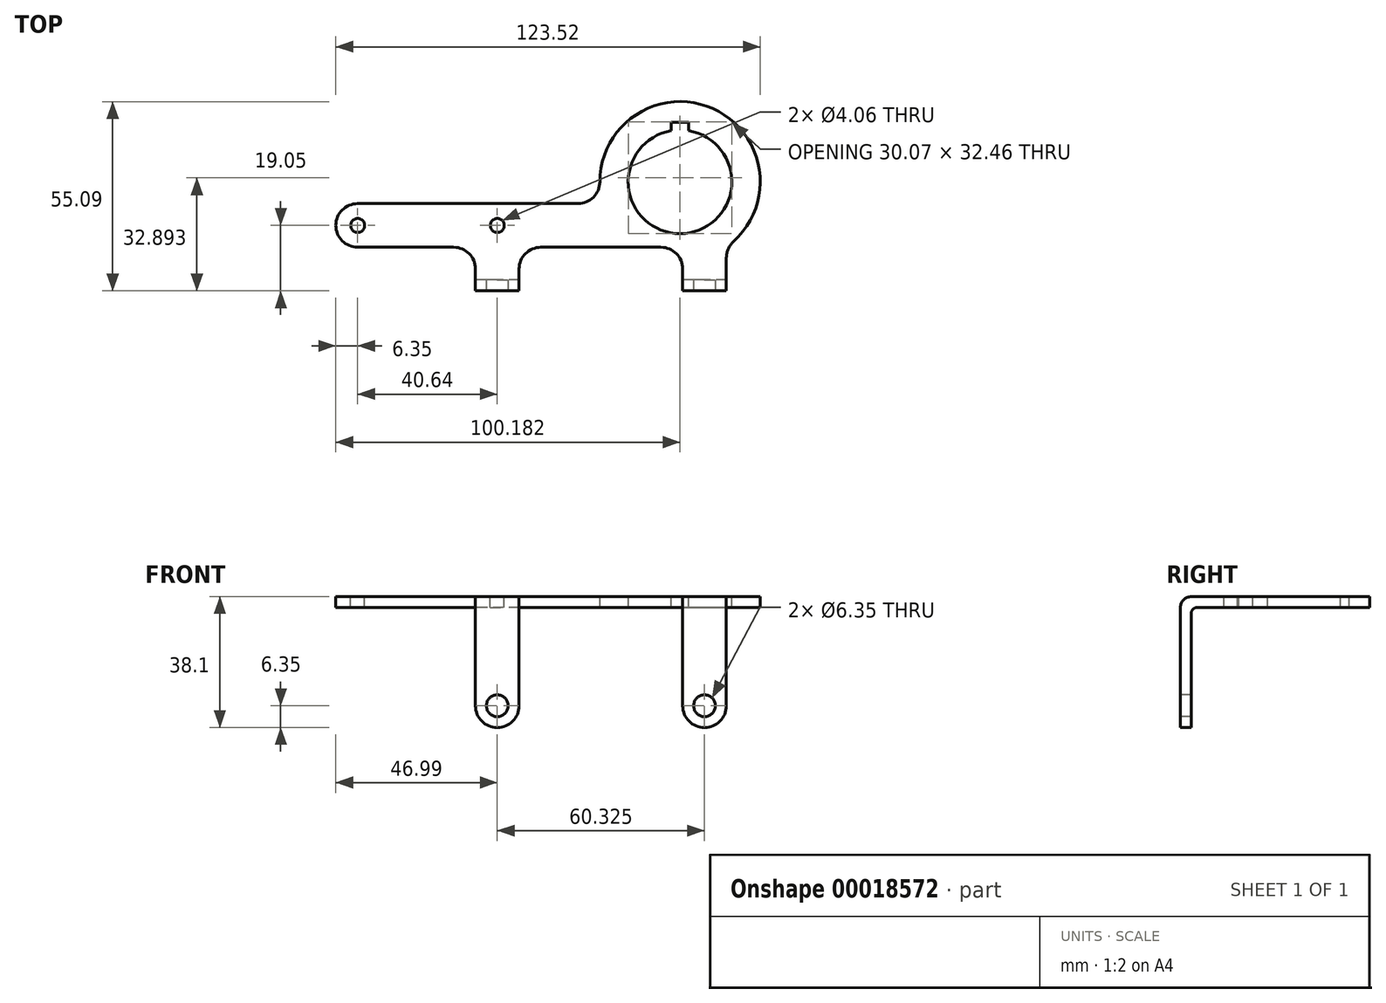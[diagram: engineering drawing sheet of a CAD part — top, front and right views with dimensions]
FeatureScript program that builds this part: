
annotation { "Feature Type Name" : "Feature", "Feature Type Description" : "" }
export const myFeature = defineFeature(function(context is Context, id is Id, definition is map)
    precondition{}
    {
        {
            var Q0;
            Q0=qCreatedBy(makeId("Right.planeOp"),FACE);
            var sketch = newSketch(context, id + "F0", { "sketchPlane" : qUnion([Q0])});
            skLineSegment(sketch, "E0", {"start": v(0, 0) * mm, "end": v(0, 38.1) * mm});
            skLineSegment(sketch, "E1", {"start": v(0, 38.1) * mm, "end": v(57.15, 38.1) * mm});
            skLineSegment(sketch, "E2", {"start": v(57.15, 38.1) * mm, "end": v(57.15, 34.93) * mm});
            skLineSegment(sketch, "E3", {"start": v(57.15, 34.93) * mm, "end": v(3.17, 34.93) * mm});
            skLineSegment(sketch, "E4", {"start": v(3.18, 34.93) * mm, "end": v(3.18, 0) * mm});
            skLineSegment(sketch, "E5", {"start": v(3.17, 0) * mm, "end": v(0, 0) * mm});
            skPoint(sketch, "E6.visualSharp", {"position": v(0, 38.1) * mm});
            skSolve(sketch);
        }
        {
            var Q0;
            Q0 = qSketchRegion(id + "F0", true);
            extrude(context, id + "F1", {"entities" : qUnion([Q0]), "depth" : 124.2 * mm});
        }
        {
            var Q0;
            Q0=makeQuery(id+"F1.opExtrude","SWEPT_EDGE",EDGE,{"disambiguationData":[OSD([sQuery(id+"F0.wireOp",EDGE,"E0"),sQuery(id+"F0.wireOp",EDGE,"E1")])]});
            fillet(context, id + "F2", {"entities" : qUnion([Q0]), "radius" : 3.17 * mm, "tangentPropagation" : true, "allowEdgeOverflow" : false});
        }
        {
            var Q0;
            Q0=makeQuery(id+"F1.opExtrude","SWEPT_EDGE",EDGE,{"disambiguationData":[OSD([sQuery(id+"F0.wireOp",EDGE,"E3"),sQuery(id+"F0.wireOp",EDGE,"E4")])]});
            fillet(context, id + "F3", {"entities" : qUnion([Q0]), "radius" : 1.59 * mm, "tangentPropagation" : true, "allowEdgeOverflow" : false});
        }
        {
            var Q0;
            Q0=makeQuery(id+"F1.opExtrude","SWEPT_FACE",FACE,{"disambiguationData":[OSD([sQuery(id+"F0.wireOp",EDGE,"E0")])]});
            var sketch = newSketch(context, id + "F4", { "sketchPlane" : qUnion([Q0])});
            skCircle(sketch, "E7", {"center": v(107.31, 6.35) * mm, "radius": 3.18 * mm});
            skCircle(sketch, "E8", {"center": v(46.99, 6.35) * mm, "radius": 3.18 * mm});
            skSolve(sketch);
        }
        {
            var Q0;
            Q0 = qSketchRegion(id + "F4", true);
            extrude(context, id + "F5", {"entities" : qUnion([Q0]), "operationType" : NewBodyOperationType.REMOVE, "endBound" : BoundingType.THROUGH_ALL, "oppositeDirection" : true, "depth" : 25.4 * mm});
        }
        {
            var Q0;
            Q0=qCreatedBy(makeId("Front.planeOp"),FACE);
            var sketch = newSketch(context, id + "F6", { "sketchPlane" : qUnion([Q0])});
            skLineSegment(sketch, "E9.bottom", {"start": v(-2.54, -2.54) * mm, "end": v(40.64, -2.54) * mm});
            skLineSegment(sketch, "E9.top", {"start": v(-2.54, 60.96) * mm, "end": v(40.64, 60.96) * mm});
            skLineSegment(sketch, "E9.left", {"start": v(-2.54, -2.54) * mm, "end": v(-2.54, 60.96) * mm});
            skLineSegment(sketch, "E9.right", {"start": v(40.64, -2.54) * mm, "end": v(40.64, 60.96) * mm});
            skLineSegment(sketch, "E10.bottom", {"start": v(53.34, -2.54) * mm, "end": v(100.97, -2.54) * mm});
            skLineSegment(sketch, "E10.top", {"start": v(53.34, 60.96) * mm, "end": v(100.97, 60.96) * mm});
            skLineSegment(sketch, "E10.left", {"start": v(53.34, -2.54) * mm, "end": v(53.34, 60.96) * mm});
            skLineSegment(sketch, "E10.right", {"start": v(100.97, -2.54) * mm, "end": v(100.97, 60.96) * mm});
            skLineSegment(sketch, "E11.bottom", {"start": v(113.67, -2.54) * mm, "end": v(126.37, -2.54) * mm});
            skLineSegment(sketch, "E11.top", {"start": v(113.67, 60.96) * mm, "end": v(126.37, 60.96) * mm});
            skLineSegment(sketch, "E11.left", {"start": v(113.67, -2.54) * mm, "end": v(113.67, 60.96) * mm});
            skLineSegment(sketch, "E11.right", {"start": v(126.37, -2.54) * mm, "end": v(126.37, 60.96) * mm});
            skSolve(sketch);
        }
        {
            var Q0;
            Q0 = qSketchRegion(id + "F6", true);
            extrude(context, id + "F7", {"entities" : qUnion([Q0]), "operationType" : NewBodyOperationType.REMOVE, "oppositeDirection" : true, "depth" : 12.7 * mm});
        }
        {
            var Q0;
            Q0=makeQuery(id+"F1.opExtrude","SWEPT_FACE",FACE,{"disambiguationData":[OSD([sQuery(id+"F0.wireOp",EDGE,"E1")])]});
            var sketch = newSketch(context, id + "F8", { "sketchPlane" : qUnion([Q0])});
            skCircle(sketch, "E12", {"center": v(6.35, 19.05) * mm, "radius": 2.03 * mm});
            skCircle(sketch, "E13", {"center": v(47, 19.05) * mm, "radius": 2.03 * mm});
            skArc(sketch, "E14", {"start": v(97.64, 46.62) * mm, "mid": v(100.18, 16.66) * mm, "end": v(102.72, 46.62) * mm});
            skLineSegment(sketch, "E15", {"start": v(100.18, 31.75) * mm, "end": v(100.18, 54.13) * mm, "construction": true});
            skLineSegment(sketch, "E16", {"start": v(100.18, 49.12) * mm, "end": v(102.72, 49.12) * mm});
            skLineSegment(sketch, "E17", {"start": v(102.72, 49.12) * mm, "end": v(102.72, 46.62) * mm});
            skLineSegment(sketch, "E18.MirrorCS", {"start": v(100.18, 49.12) * mm, "end": v(97.64, 49.12) * mm});
            skLineSegment(sketch, "E19.MirrorCS", {"start": v(97.64, 49.12) * mm, "end": v(97.64, 46.62) * mm});
            skSolve(sketch);
        }
        {
            var Q0;
            Q0 = qSketchRegion(id + "F8", true);
            extrude(context, id + "F9", {"entities" : qUnion([Q0]), "operationType" : NewBodyOperationType.REMOVE, "endBound" : BoundingType.THROUGH_ALL, "oppositeDirection" : true, "depth" : 25.4 * mm});
        }
        {
            var Q0;
            Q0=makeQuery(id+"F1.opExtrude","SWEPT_FACE",FACE,{"disambiguationData":[OSD([sQuery(id+"F0.wireOp",EDGE,"E1")])]});
            var sketch = newSketch(context, id + "F10", { "sketchPlane" : qUnion([Q0])});
            skLineSegment(sketch, "E20.bottom", {"start": v(-2.54, 63.5) * mm, "end": v(127, 63.5) * mm});
            skLineSegment(sketch, "E20.top", {"start": v(-2.54, 25.4) * mm, "end": v(77.72, 25.4) * mm});
            skLineSegment(sketch, "E20.left", {"start": v(-2.54, 63.5) * mm, "end": v(-2.54, 25.4) * mm});
            skArc(sketch, "E21", {"start": v(113.67, 12.7) * mm, "mid": v(107.96, 53.76) * mm, "end": v(77.72, 25.4) * mm});
            skLineSegment(sketch, "E22", {"start": v(113.67, 12.7) * mm, "end": v(113.67, 6.35) * mm});
            skLineSegment(sketch, "E23", {"start": v(113.67, 6.35) * mm, "end": v(127, 6.35) * mm});
            skLineSegment(sketch, "E24", {"start": v(127, 6.35) * mm, "end": v(127, 63.5) * mm});
            skSolve(sketch);
        }
        {
            var Q0;
            Q0 = qSketchRegion(id + "F10", true);
            extrude(context, id + "F11", {"entities" : qUnion([Q0]), "operationType" : NewBodyOperationType.REMOVE, "endBound" : BoundingType.THROUGH_ALL, "oppositeDirection" : true, "depth" : 25.4 * mm});
        }
        {
            var Q0;
            Q0=makeQuery(id+"F7.boolean.opBoolean","INTERSECT",EDGE,{"derivedFrom":[makeQuery(id+"F1.opExtrude","SWEPT_FACE",FACE,{"disambiguationData":[OSD([sQuery(id+"F0.wireOp",EDGE,"E5")])]}),makeQuery(id+"F7.opExtrude","SWEPT_FACE",FACE,{"disambiguationData":[OSD([sQuery(id+"F6.wireOp",EDGE,"E10.left")])]})]});
            var Q1;
            Q1=makeQuery(id+"F7.boolean.opBoolean","INTERSECT",EDGE,{"derivedFrom":[makeQuery(id+"F1.opExtrude","SWEPT_FACE",FACE,{"disambiguationData":[OSD([sQuery(id+"F0.wireOp",EDGE,"E5")])]}),makeQuery(id+"F7.opExtrude","SWEPT_FACE",FACE,{"disambiguationData":[OSD([sQuery(id+"F6.wireOp",EDGE,"E11.left")])]})]});
            var Q2;
            Q2=makeQuery(id+"F7.boolean.opBoolean","INTERSECT",EDGE,{"derivedFrom":[makeQuery(id+"F1.opExtrude","SWEPT_FACE",FACE,{"disambiguationData":[OSD([sQuery(id+"F0.wireOp",EDGE,"E5")])]}),makeQuery(id+"F7.opExtrude","SWEPT_FACE",FACE,{"disambiguationData":[OSD([sQuery(id+"F6.wireOp",EDGE,"E10.right")])]})]});
            var Q3;
            Q3=makeQuery(id+"F7.boolean.opBoolean","INTERSECT",EDGE,{"derivedFrom":[makeQuery(id+"F1.opExtrude","SWEPT_FACE",FACE,{"disambiguationData":[OSD([sQuery(id+"F0.wireOp",EDGE,"E5")])]}),makeQuery(id+"F7.opExtrude","SWEPT_FACE",FACE,{"disambiguationData":[OSD([sQuery(id+"F6.wireOp",EDGE,"E9.right")])]})]});
            var Q4;
            Q4=makeQuery(id+"F7.boolean.opBoolean","COPY",EDGE,{"derivedFrom":makeQuery(id+"F7.opExtrude","CAP_EDGE",EDGE,{"disambiguationData":[OSD([sQuery(id+"F6.wireOp",EDGE,"E9.right")])],"isStart":false})});
            var Q5;
            Q5=makeQuery(id+"F7.boolean.opBoolean","COPY",EDGE,{"derivedFrom":makeQuery(id+"F7.opExtrude","CAP_EDGE",EDGE,{"disambiguationData":[OSD([sQuery(id+"F6.wireOp",EDGE,"E10.left")])],"isStart":false})});
            var Q6;
            Q6=makeQuery(id+"F7.boolean.opBoolean","COPY",EDGE,{"derivedFrom":makeQuery(id+"F7.opExtrude","CAP_EDGE",EDGE,{"disambiguationData":[OSD([sQuery(id+"F6.wireOp",EDGE,"E10.right")])],"isStart":false})});
            var Q7;
            Q7=makeQuery(id+"F7.boolean.opBoolean","INTERSECT",EDGE,{"derivedFrom":[makeQuery(id+"F1.opExtrude","CAP_FACE",FACE,{"disambiguationData":[OSD([sQuery(id+"F0.wireOp",EDGE,"E0"),sQuery(id+"F0.wireOp",EDGE,"E1"),sQuery(id+"F0.wireOp",EDGE,"E2"),sQuery(id+"F0.wireOp",EDGE,"E3"),sQuery(id+"F0.wireOp",EDGE,"E4"),sQuery(id+"F0.wireOp",EDGE,"E5")])],"isStart":true}),makeQuery(id+"F7.opExtrude","CAP_FACE",FACE,{"disambiguationData":[OSD([sQuery(id+"F6.wireOp",EDGE,"E9.bottom"),sQuery(id+"F6.wireOp",EDGE,"E9.top"),sQuery(id+"F6.wireOp",EDGE,"E9.left"),sQuery(id+"F6.wireOp",EDGE,"E9.right")])],"isStart":false})]});
            var Q8;
            Q8=makeQuery(id+"F11.boolean.opBoolean","INTERSECT",EDGE,{"derivedFrom":[makeQuery(id+"F1.opExtrude","CAP_FACE",FACE,{"disambiguationData":[OSD([sQuery(id+"F0.wireOp",EDGE,"E0"),sQuery(id+"F0.wireOp",EDGE,"E1"),sQuery(id+"F0.wireOp",EDGE,"E2"),sQuery(id+"F0.wireOp",EDGE,"E3"),sQuery(id+"F0.wireOp",EDGE,"E4"),sQuery(id+"F0.wireOp",EDGE,"E5")])],"isStart":true}),makeQuery(id+"F11.opExtrude","SWEPT_FACE",FACE,{"disambiguationData":[OSD([sQuery(id+"F10.wireOp",EDGE,"E20.top")])]})]});
            var Q9;
            Q9=makeQuery(id+"F11.boolean.opBoolean","COPY",EDGE,{"derivedFrom":makeQuery(id+"F11.opExtrude","SWEPT_EDGE",EDGE,{"disambiguationData":[OSD([sQuery(id+"F10.wireOp",EDGE,"E20.top"),sQuery(id+"F10.wireOp",EDGE,"f17af5c3-7e73-4e9e-9507-6560ecef05da")])]})});
            var Q10;
            Q10=makeQuery(id+"F11.boolean.opBoolean","COPY",EDGE,{"derivedFrom":makeQuery(id+"F11.opExtrude","SWEPT_EDGE",EDGE,{"disambiguationData":[OSD([sQuery(id+"F10.wireOp",EDGE,"bb1fc792-87ea-4b88-bd3f-a6e104640378"),sQuery(id+"F10.wireOp",EDGE,"0afa1586-cc7e-4993-a398-f57e6e3e4493")])]})});
            var Q11;
            {var subQ0=sQuery(id+"F6.wireOp",EDGE,"E11.left");Q11=makeQuery(id+"F11.boolean.opBoolean","MERGE",EDGE,{"derivedFrom":[makeQuery(id+"F7.boolean.opBoolean","COPY",EDGE,{"derivedFrom":makeQuery(id+"F7.opExtrude","CAP_EDGE",EDGE,{"disambiguationData":[OSD([subQ0])],"isStart":false})}),makeQuery(id+"F11.opExtrude","SWEPT_EDGE",EDGE,{"disambiguationData":[OSD([sQuery(id+"F0.wireOp",EDGE,"E1"),sQuery(id+"F6.wireOp",EDGE,"E11.bottom"),sQuery(id+"F6.wireOp",EDGE,"E11.top"),subQ0,sQuery(id+"F6.wireOp",EDGE,"E11.right"),sQuery(id+"F10.wireOp",EDGE,"E21"),sQuery(id+"F10.wireOp",EDGE,"E22")])]})]});}
            fillet(context, id + "F12", {"entities" : qUnion([Q0, Q1, Q2, Q3, Q4, Q5, Q6, Q7, Q8, Q9, Q10, Q11]), "radius" : 6.35 * mm, "tangentPropagation" : true, "allowEdgeOverflow" : false});
        }
        {
            var Q0;
            Q0=makeQuery(id+"F1.opExtrude","SWEPT_BODY",BODY,{"disambiguationData":[OSD([sQuery(id+"F0.wireOp",EDGE,"E0"),sQuery(id+"F0.wireOp",EDGE,"E1"),sQuery(id+"F0.wireOp",EDGE,"E2"),sQuery(id+"F0.wireOp",EDGE,"E3"),sQuery(id+"F0.wireOp",EDGE,"E4"),sQuery(id+"F0.wireOp",EDGE,"E5")])]});
            transform(context, id + "F13", {"entities" : qUnion([Q0]), "transformType" : TransformType.TRANSLATION_3D, "dx" : 0 * mm, "dy" : 0 * mm, "dz" : 0 * mm, "makeCopy" : true});
        }
        {
            var Q0;
            Q0=makeQuery(id+"F13.opPattern","COPY",BODY,{"derivedFrom":makeQuery(id+"F1.opExtrude","SWEPT_BODY",BODY,{"disambiguationData":[OSD([sQuery(id+"F0.wireOp",EDGE,"E0"),sQuery(id+"F0.wireOp",EDGE,"E1"),sQuery(id+"F0.wireOp",EDGE,"E2"),sQuery(id+"F0.wireOp",EDGE,"E3"),sQuery(id+"F0.wireOp",EDGE,"E4"),sQuery(id+"F0.wireOp",EDGE,"E5")])]}),"instanceName":"1"});
            deleteBodies(context, id + "F14", {"entities" : qUnion([Q0])});
        }
    });
